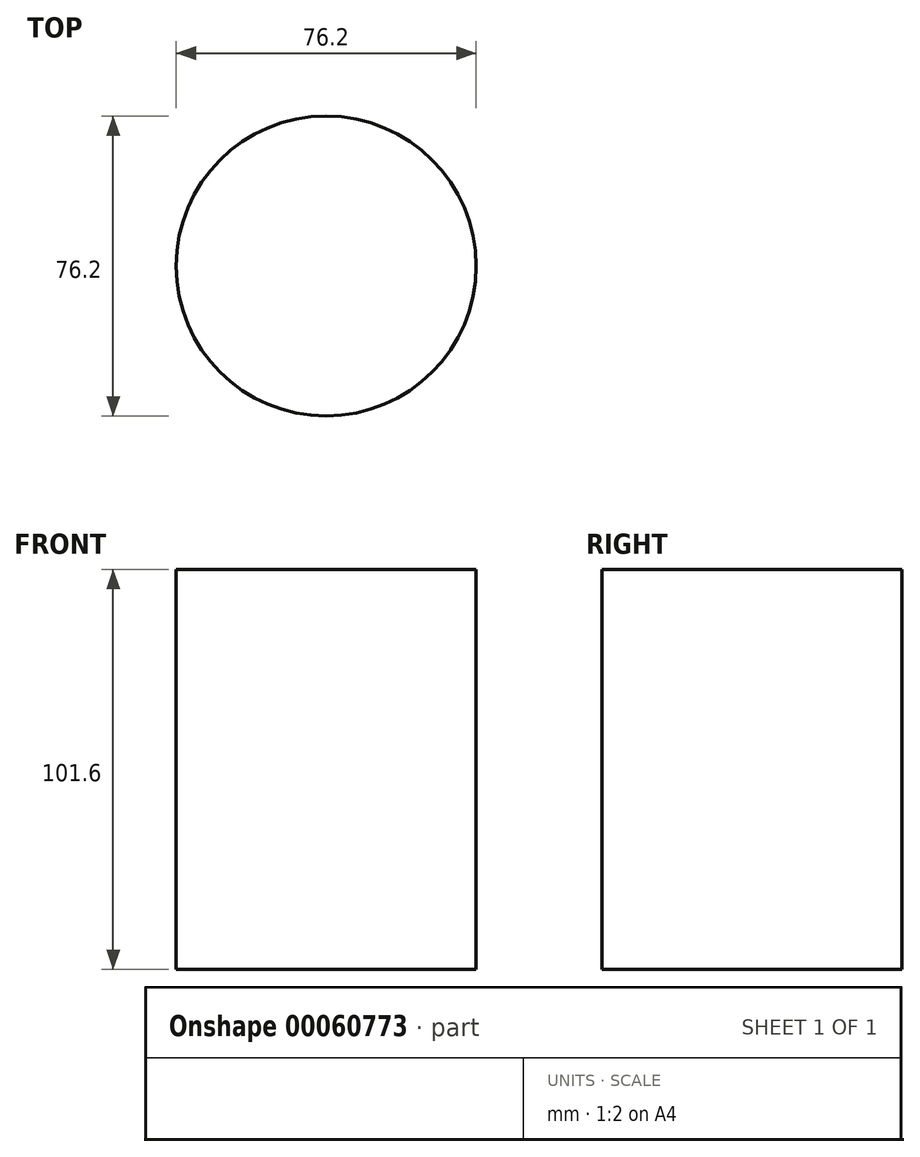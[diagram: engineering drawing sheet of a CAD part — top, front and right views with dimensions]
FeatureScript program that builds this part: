
annotation { "Feature Type Name" : "Feature", "Feature Type Description" : "" }
export const myFeature = defineFeature(function(context is Context, id is Id, definition is map)
    precondition{}
    {
        {
            var Q0;
            Q0=qCreatedBy(makeId("Top.planeOp"),FACE);
            var sketch = newSketch(context, id + "F0", { "sketchPlane" : qUnion([Q0])});
            skCircle(sketch, "E0", {"center": v(0, 0) * mm, "radius": 38.1 * mm});
            skSolve(sketch);
        }
        {
            var Q0;
            Q0 = qSketchRegion(id + "F0", true);
            extrude(context, id + "F1", {"entities" : qUnion([Q0]), "endBound" : BoundingType.SYMMETRIC, "depth" : 101.6 * mm});
        }
    });
